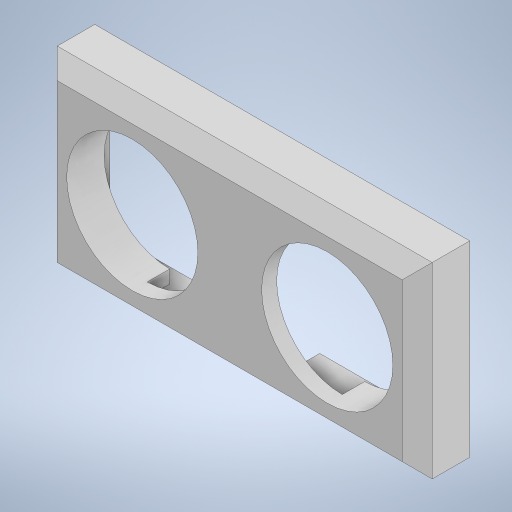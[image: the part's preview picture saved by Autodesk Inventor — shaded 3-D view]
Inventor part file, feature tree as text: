
AUTODESK INVENTOR PART (.ipt)
format: ipt  version: 2024.2 (Build 282272000, 272)  size: 276,480 bytes
history: native  units: mm
features: extrude x3, sketch x3, chamfer x1
ambient origin geometry x8: Origin, YZ Plane, XZ Plane, XY Plane, X Axis, Y Axis, Z Axis, Center Point
bodies: Solid1 (feature_tree)
feature tree (7):
  extrude  "Extrusion1"  Depth=17.5mm
  extrude  "Extrusion2"  Depth=50.0mm
  extrude  "Extrusion3"  Depth=12.0mm
  chamfer  "Chamfer2"  Distance=12.5mm
  sketch  "Sketch1"  dims[d0=17.5mm d1=17.5mm]
  sketch  "Sketch2"  dims[d2=26.0mm d3=50.0mm]
  sketch  "Sketch3"  dims[d4=25.0mm d5=12.0mm d6=12.5mm d7=2.0mm d8=0.0mm d12=2.0mm d14=46.0mm d15=2.0mm d16=21.0mm d17=5.0mm d18=0.0mm d19=10.0mm d20=20.0mm d21=2.0mm d22=2.0mm d23=25.0mm d24=3.0mm d25=0.0mm d26=2.0mm d27=2.0mm d28=45.0deg]
